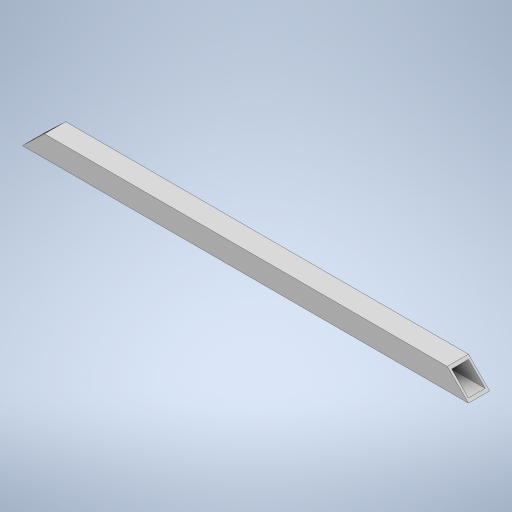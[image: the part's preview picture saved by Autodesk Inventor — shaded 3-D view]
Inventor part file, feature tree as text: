
AUTODESK INVENTOR PART (.ipt)
format: ipt  version: 2024.3 (Build 283343000, 343)  size: 250,368 bytes
history: native  units: mm
features: extrude x2, sketch x2
ambient origin geometry x8: Origin, YZ Plane, XZ Plane, XY Plane, X Axis, Y Axis, Z Axis, Center Point
bodies: Solid1 (feature_tree)
feature tree (4):
  extrude  "Extrusion1"  Depth=2.0mm
  extrude  "Extrusion2"  Depth=19.0mm
  sketch  "Sketch1"  dims[d0=2.0mm d1=2.0mm]
  sketch  "Sketch2"  dims[d2=19.0mm d3=19.0mm d4=400.0mm d5=0.0mm d6=19.89194mm d7=19.0mm d8=10.0mm d9=0.0mm]
